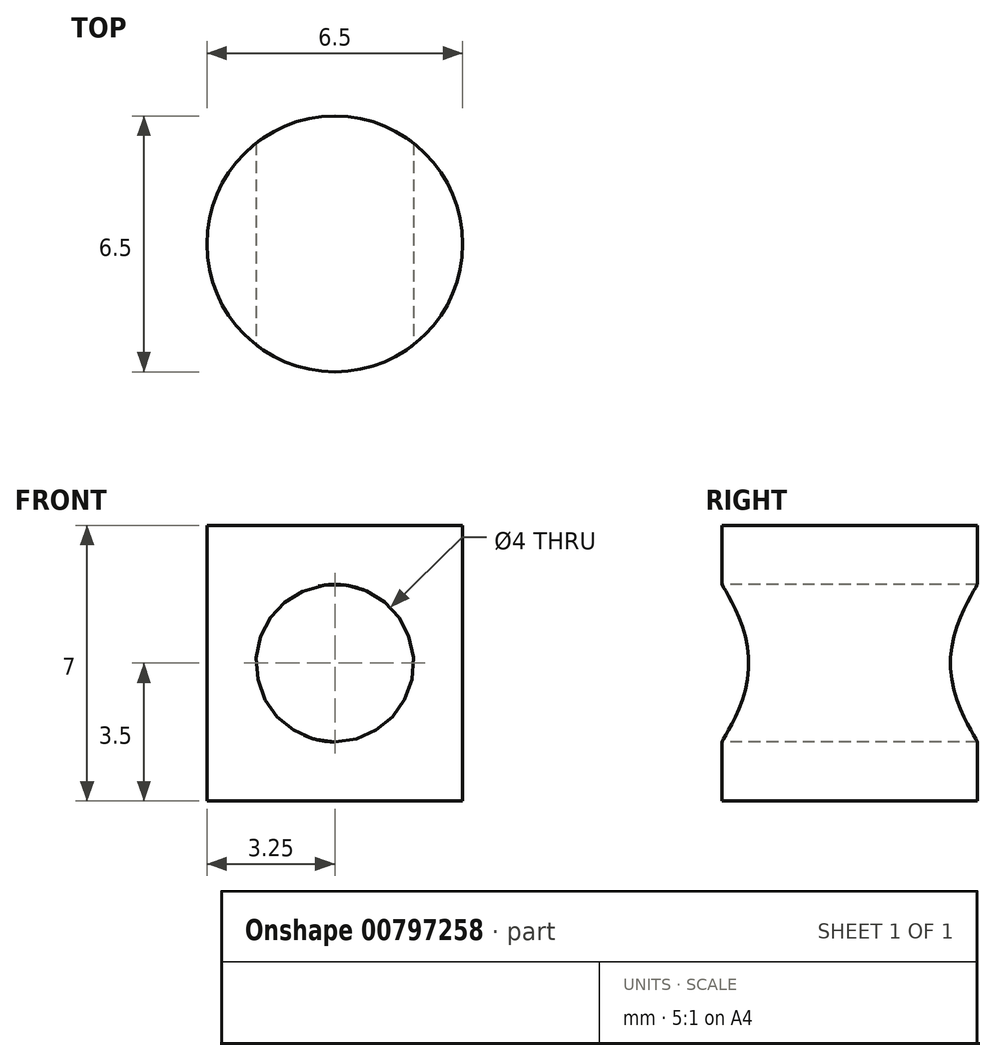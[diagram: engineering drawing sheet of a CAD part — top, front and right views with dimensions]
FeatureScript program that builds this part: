
annotation { "Feature Type Name" : "Feature", "Feature Type Description" : "" }
export const myFeature = defineFeature(function(context is Context, id is Id, definition is map)
    precondition{}
    {
        {
            var Q0;
            Q0=qCreatedBy(makeId("Top.planeOp"),FACE);
            var sketch = newSketch(context, id + "F0", { "sketchPlane" : qUnion([Q0])});
            skCircle(sketch, "E0", {"center": v(0, 0) * mm, "radius": 3.25 * mm});
            skSolve(sketch);
        }
        {
            var Q0;
            Q0 = qSketchRegion(id + "F0", true);
            extrude(context, id + "F1", {"entities" : qUnion([Q0]), "depth" : 7 * mm, "offsetDistance" : 25 * mm});
        }
        {
            var Q0;
            Q0=qCreatedBy(makeId("Front.planeOp"),FACE);
            var sketch = newSketch(context, id + "F2", { "sketchPlane" : qUnion([Q0])});
            skCircle(sketch, "E1", {"center": v(0, 3.5) * mm, "radius": 2 * mm});
            skSolve(sketch);
        }
        {
            var Q0;
            Q0 = qSketchRegion(id + "F2", true);
            extrude(context, id + "F3", {"entities" : qUnion([Q0]), "operationType" : NewBodyOperationType.REMOVE, "endBound" : BoundingType.THROUGH_ALL, "oppositeDirection" : true, "depth" : 25 * mm, "offsetDistance" : 25 * mm, "hasSecondDirection" : true, "secondDirectionBound" : SecondDirectionBoundingType.THROUGH_ALL, "secondDirectionOppositeDirection" : false, "secondDirectionDepth" : 25 * mm});
        }
    });
